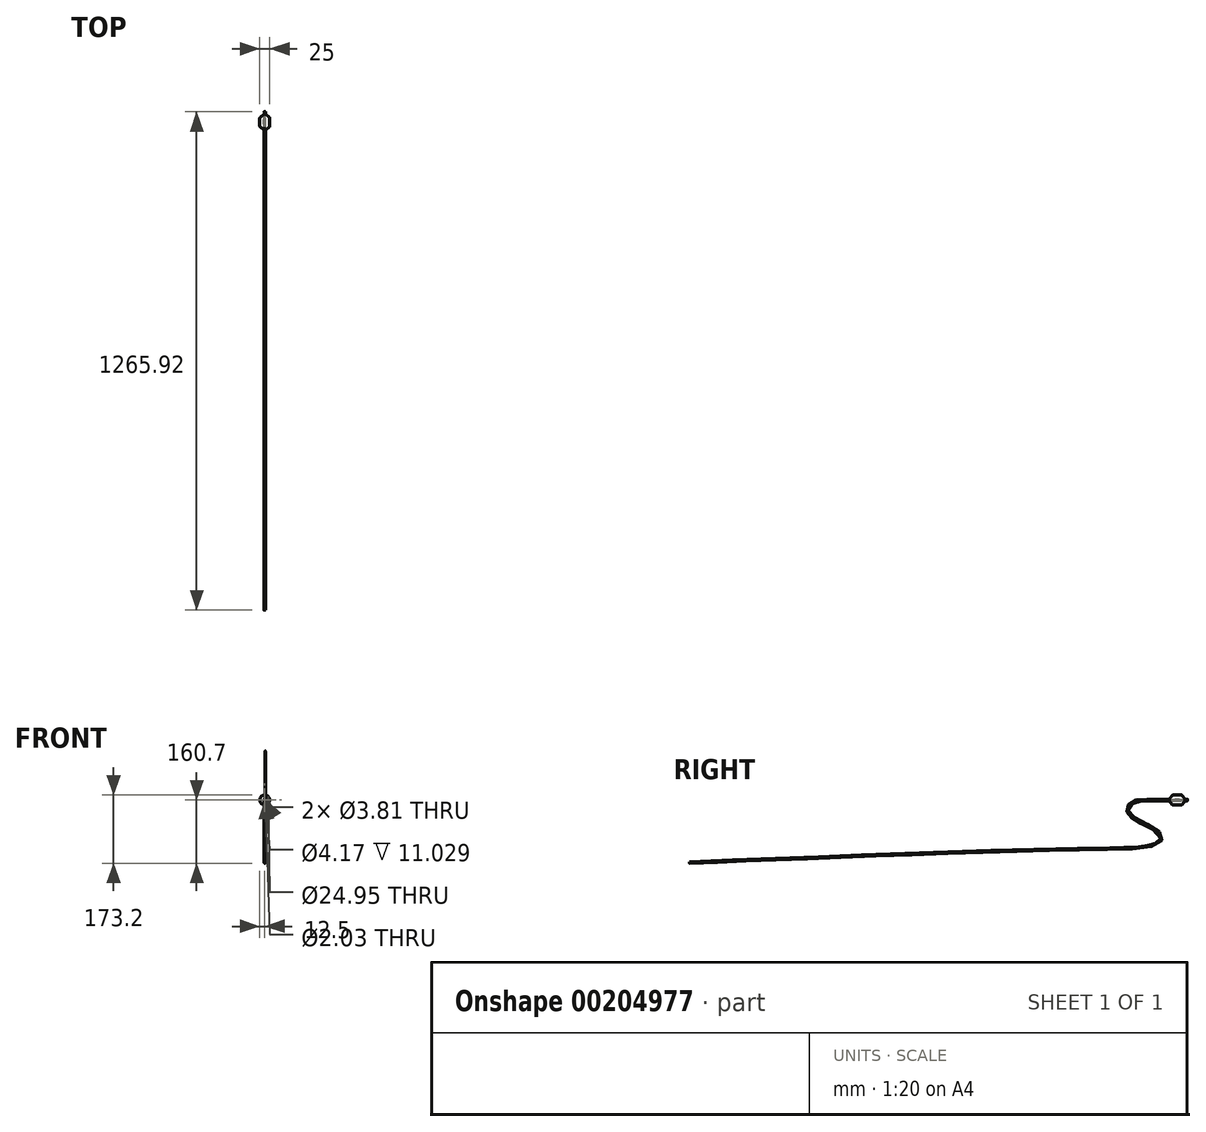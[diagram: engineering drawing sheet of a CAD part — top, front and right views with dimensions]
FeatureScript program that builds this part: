
annotation { "Feature Type Name" : "Feature", "Feature Type Description" : "" }
export const myFeature = defineFeature(function(context is Context, id is Id, definition is map)
    precondition{}
    {
        {
            var Q0;
            Q0=qCreatedBy(makeId("Front.planeOp"),FACE);
            var sketch = newSketch(context, id + "F0", { "sketchPlane" : qUnion([Q0])});
            skCircle(sketch, "E0", {"center": v(0, 0) * mm, "radius": 1.02 * mm});
            skCircle(sketch, "E1", {"center": v(0, 0) * mm, "radius": 1.9 * mm});
            skSolve(sketch);
        }
        {
            var Q0;
            Q0=makeQuery(id+"F0.imprint","IMPRINT",FACE,{"disambiguationData":[TD([[makeQuery(id+"F0.imprint","IMPRINT",EDGE,{"derivedFrom":sQuery(id+"F0.wireOp",EDGE,"E0")}),-1.0]])]});
            extrude(context, id + "F1", {"entities" : qUnion([Q0]), "depth" : 76.2 * mm, "offsetDistance" : 25.4 * mm});
        }
        {
            var Q0;
            Q0=makeQuery(id+"F1.opExtrude","CAP_EDGE",EDGE,{"disambiguationData":[OSD([sQuery(id+"F0.wireOp",EDGE,"E0")])],"isStart":true});
            chamfer(context, id + "F2", {"entities" : qUnion([Q0]), "width" : 0.56 * mm, "tangentPropagation" : true});
        }
        {
            var Q0;
            Q0=makeQuery(id+"F1.opExtrude","CAP_EDGE",EDGE,{"disambiguationData":[OSD([sQuery(id+"F0.wireOp",EDGE,"E1")])],"isStart":true});
            fillet(context, id + "F3", {"entities" : qUnion([Q0]), "radius" : 0.13 * mm, "tangentPropagation" : true, "allowEdgeOverflow" : false});
        }
        {
            var Q0;
            Q0=qCreatedBy(makeId("Right.planeOp"),FACE);
            var sketch = newSketch(context, id + "F4", { "sketchPlane" : qUnion([Q0])});
            skLineSegment(sketch, "E2", {"start": v(0, 0) * mm, "end": v(-318.3, 0) * mm, "construction": true});
            skSolve(sketch);
        }
        {
            var Q0;
            Q0=qCreatedBy(makeId("Right.planeOp"),FACE);
            var sketch = newSketch(context, id + "F5", { "sketchPlane" : qUnion([Q0])});
            skLineSegment(sketch, "E3.0", {"start": v(-253.87, 0) * mm, "end": v(-253.87, -1.9) * mm, "construction": true});
            skLineSegment(sketch, "E4", {"start": v(-46.36, 1.9) * mm, "end": v(-46.32, 1.9) * mm});
            skLineSegment(sketch, "E5", {"start": v(-46.35, 1.9) * mm, "end": v(-39.37, 11) * mm});
            skLineSegment(sketch, "E6", {"start": v(-36.35, 12.5) * mm, "end": v(-16.36, 12.5) * mm});
            skLineSegment(sketch, "E7", {"start": v(-13.33, 11) * mm, "end": v(-6.35, 1.9) * mm});
            skLineSegment(sketch, "E8.0", {"start": v(0, 0) * mm, "end": v(-318.3, 0) * mm, "construction": true});
            skLineSegment(sketch, "E9", {"start": v(-46.32, 1.9) * mm, "end": v(-39.36, 10.98) * mm});
            skLineSegment(sketch, "E10", {"start": v(-36.33, 12.47) * mm, "end": v(-16.37, 12.47) * mm});
            skLineSegment(sketch, "E11", {"start": v(-13.35, 10.98) * mm, "end": v(-6.38, 1.9) * mm});
            skLineSegment(sketch, "E12.trimOffspring", {"start": v(-6.38, 1.9) * mm, "end": v(-6.35, 1.9) * mm});
            skPoint(sketch, "E13.orphan", {"position": v(-253.87, 1.9) * mm});
            skPoint(sketch, "E14.orphan", {"position": v(-38.23, 1.9) * mm});
            skPoint(sketch, "E15.visualSharp", {"position": v(-38.23, 12.5) * mm});
            skArc(sketch, "E15.filletArc", {"start": v(-36.35, 12.5) * mm, "mid": v(-38.03, 12.1) * mm, "end": v(-39.37, 11) * mm});
            skPoint(sketch, "E16.visualSharp", {"position": v(-38.21, 12.47) * mm});
            skArc(sketch, "E16.filletArc", {"start": v(-36.33, 12.47) * mm, "mid": v(-38.02, 12.08) * mm, "end": v(-39.36, 10.98) * mm});
            skPoint(sketch, "E17.visualSharp", {"position": v(-14.5, 12.47) * mm});
            skArc(sketch, "E17.filletArc", {"start": v(-13.35, 10.98) * mm, "mid": v(-14.68, 12.08) * mm, "end": v(-16.37, 12.47) * mm});
            skPoint(sketch, "E18.visualSharp", {"position": v(-14.48, 12.5) * mm});
            skArc(sketch, "E18.filletArc", {"start": v(-13.33, 11) * mm, "mid": v(-14.67, 12.1) * mm, "end": v(-16.36, 12.5) * mm});
            skLineSegment(sketch, "E19", {"start": v(-26.35, 12.5) * mm, "end": v(-26.35, -17.87) * mm, "construction": true});
            skSolve(sketch);
        }
        {
            var Q0;
            Q0=qSketchRegion(id+"F5",true);
            var Q1;
            Q1=sQuery(id+"F5.wireOp",EDGE,"E8.0");
            revolve(context, id + "F6", {"entities" : qUnion([Q0]), "axis" : qUnion([Q1]), "revolveType" : RevolveType.FULL});
        }
        {
            var Q0;
            Q0=qCreatedBy(makeId("Front.planeOp"),FACE);
            cPlane(context, id + "F7", {"entities" : qUnion([Q0]), "cplaneType" : CPlaneType.OFFSET, "offset" : 20.42 * mm, "width" : 152.4 * mm, "height" : 152.4 * mm});
        }
        {
            var Q0;
            Q0=qCreatedBy(makeId("Front.planeOp"),FACE);
            cPlane(context, id + "F8", {"entities" : qUnion([Q0]), "cplaneType" : CPlaneType.OFFSET, "offset" : 31.45 * mm, "width" : 152.4 * mm, "height" : 152.4 * mm});
        }
        {
            var Q0;
            Q0=qCreatedBy(id+"F8.planeOp",FACE);
            var sketch = newSketch(context, id + "F9", { "sketchPlane" : qUnion([Q0])});
            skCircle(sketch, "E20.0", {"center": v(0, 0) * mm, "radius": 12.5 * mm, "construction": true});
            skArc(sketch, "E21", {"start": v(-10.13, 7.33) * mm, "mid": v(0, 12.5) * mm, "end": v(10.13, 7.33) * mm});
            skLineSegment(sketch, "E22", {"start": v(0, 18.59) * mm, "end": v(0, -14.82) * mm, "construction": true});
            skLineSegment(sketch, "E23", {"start": v(-18.7, 0) * mm, "end": v(23.1, 0) * mm, "construction": true});
            skArc(sketch, "E24.MirrorCS", {"start": v(-10.13, -7.33) * mm, "mid": v(0, -12.5) * mm, "end": v(10.13, -7.33) * mm});
            skArc(sketch, "E25", {"start": v(-10.55, 6.7) * mm, "mid": v(-12.5, 0) * mm, "end": v(-10.55, -6.7) * mm});
            skArc(sketch, "E26.MirrorCS", {"start": v(10.55, 6.7) * mm, "mid": v(12.5, 0) * mm, "end": v(10.55, -6.7) * mm});
            skSolve(sketch);
        }
        {
            var Q0;
            Q0=qCreatedBy(id+"F7.planeOp",FACE);
            var sketch = newSketch(context, id + "F10", { "sketchPlane" : qUnion([Q0])});
            skCircle(sketch, "E27.0", {"center": v(0, 0) * mm, "radius": 12.5 * mm, "construction": true});
            skArc(sketch, "E28", {"start": v(-10.13, 7.33) * mm, "mid": v(0, 12.5) * mm, "end": v(10.13, 7.33) * mm});
            skLineSegment(sketch, "E29", {"start": v(0, 18.32) * mm, "end": v(0, -15.1) * mm, "construction": true});
            skLineSegment(sketch, "E30", {"start": v(-19.02, 0) * mm, "end": v(22.78, 0) * mm, "construction": true});
            skArc(sketch, "E31.MirrorCS", {"start": v(-10.13, -7.33) * mm, "mid": v(0, -12.5) * mm, "end": v(10.13, -7.33) * mm});
            skArc(sketch, "E32", {"start": v(-10.55, 6.7) * mm, "mid": v(-12.5, 0) * mm, "end": v(-10.55, -6.7) * mm});
            skArc(sketch, "E33.MirrorCS", {"start": v(10.55, 6.7) * mm, "mid": v(12.5, 0) * mm, "end": v(10.55, -6.7) * mm});
            skSolve(sketch);
        }
        {
            var Q0;
            Q0=qCreatedBy(id+"F7.planeOp",FACE);
            var sketch = newSketch(context, id + "F11", { "sketchPlane" : qUnion([Q0])});
            skCircle(sketch, "E34", {"center": v(0, 0) * mm, "radius": 2.47 * mm});
            skCircle(sketch, "E35", {"center": v(0, 0) * mm, "radius": 2.08 * mm});
            skSolve(sketch);
        }
        {
            var Q0;
            Q0 = qSketchRegion(id + "F11", true);
            var Q1;
            Q1=qCreatedBy(id+"F8.planeOp",FACE);
            extrude(context, id + "F12", {"entities" : qUnion([Q0]), "operationType" : NewBodyOperationType.ADD, "endBound" : BoundingType.UP_TO_SURFACE, "endBoundEntityFace" : qUnion([Q1]), "depth" : 25.4 * mm});
        }
        {
            var Q0;
            Q0=qCreatedBy(makeId("Right.planeOp"),FACE);
            cPlane(context, id + "F13", {"entities" : qUnion([Q0]), "cplaneType" : CPlaneType.OFFSET, "offset" : 1.9 * mm, "oppositeDirection" : true, "width" : 152.4 * mm, "height" : 152.4 * mm});
        }
        {
            var Q0;
            Q0=qCreatedBy(id+"F13.planeOp",FACE);
            var sketch = newSketch(context, id + "F14", { "sketchPlane" : qUnion([Q0])});
            skFitSpline(sketch, "E36", {"points": [v(-76.2, 0) * mm, v(-139.75, -6.2) * mm, v(-153.35, -26.18) * mm, v(-120.57, -55.78) * mm, v(-67.66, -88.23) * mm, v(-73, -108.14) * mm, v(-204.77, -123.54) * mm, v(-542.84, -131.77) * mm, v(-966.12, -147.53) * mm, v(-1265.85, -158.8) * mm], "startDerivative": vector(-1224.39, 0) * mm, "endDerivative": vector(-1629.33, -59.79) * mm});
            skLineSegment(sketch, "E37.0", {"start": v(-76.2, -1.9) * mm, "end": v(-76.2, 1.9) * mm, "construction": true});
            skSolve(sketch);
        }
        {
            var Q0;
            Q0=makeQuery(id+"F1.opExtrude","CAP_FACE",FACE,{"disambiguationData":[OSD([sQuery(id+"F0.wireOp",EDGE,"E0"),sQuery(id+"F0.wireOp",EDGE,"E1")])],"isStart":false});
            cPlane(context, id + "F15", {"entities" : qUnion([Q0]), "cplaneType" : CPlaneType.OFFSET, "offset" : 0 * mm, "width" : 152.4 * mm, "height" : 152.4 * mm});
        }
        {
            var Q0;
            Q0=qCreatedBy(id+"F15.planeOp",FACE);
            var sketch = newSketch(context, id + "F16", { "sketchPlane" : qUnion([Q0])});
            skCircle(sketch, "E38.0", {"center": v(0, 0) * mm, "radius": 1.9 * mm});
            skCircle(sketch, "E39.0", {"center": v(0, 0) * mm, "radius": 1.02 * mm});
            skSolve(sketch);
        }
        {
            var Q0;
            Q0 = qSketchRegion(id + "F16", true);
            var Q1;
            Q1 = qConstructionFilter(qBodyType(qCreatedBy(id + "F14" ,EDGE), BodyType.WIRE), ConstructionObject.NO);
            sweep(context, id + "F17", {"operationType" : NewBodyOperationType.ADD, "profiles" : qUnion([Q0]), "path" : qUnion([Q1])});
        }
    });
